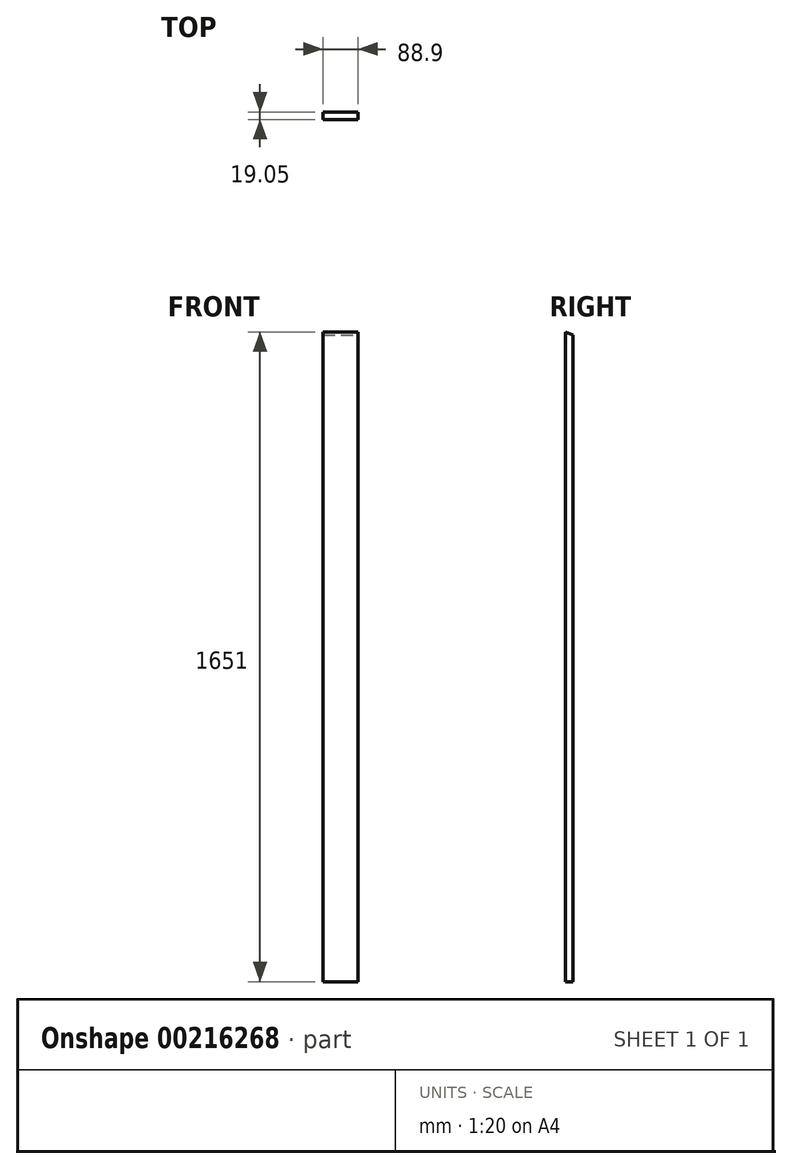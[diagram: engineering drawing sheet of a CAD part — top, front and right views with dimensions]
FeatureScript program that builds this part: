
annotation { "Feature Type Name" : "Feature", "Feature Type Description" : "" }
export const myFeature = defineFeature(function(context is Context, id is Id, definition is map)
    precondition{}
    {
        {
            var Q0;
            Q0=qCreatedBy(makeId("Front.planeOp"),FACE);
            var sketch = newSketch(context, id + "F0", { "sketchPlane" : qUnion([Q0])});
            skLineSegment(sketch, "E0", {"start": v(-3025.56, -1512.47) * mm, "end": v(-3114.46, -1512.47) * mm});
            skLineSegment(sketch, "E1", {"start": v(-3114.46, -1512.47) * mm, "end": v(-3114.46, 138.53) * mm});
            skLineSegment(sketch, "E2", {"start": v(-3114.46, 138.53) * mm, "end": v(-3025.56, 138.53) * mm});
            skLineSegment(sketch, "E3", {"start": v(-3025.56, 138.53) * mm, "end": v(-3025.56, -1512.47) * mm});
            skSolve(sketch);
        }
        {
            var Q0;
            Q0=makeQuery(id+"F0.imprint","IMPRINT",FACE,{"disambiguationData":[TD([[makeQuery(id+"F0.imprint","IMPRINT",EDGE,{"derivedFrom":sQuery(id+"F0.wireOp",EDGE,"E0")}),-1.0]])]});
            extrude(context, id + "F1", {"entities" : qUnion([Q0]), "depth" : 19.05 * mm});
        }
        {
            var Q0;
            Q0=makeQuery(id+"F1.opExtrude","SWEPT_FACE",FACE,{"disambiguationData":[OSD([sQuery(id+"F0.wireOp",EDGE,"E3")])]});
            var sketch = newSketch(context, id + "F2", { "sketchPlane" : qUnion([Q0])});
            skLineSegment(sketch, "E4", {"start": v(-19.05, 138.53) * mm, "end": v(0, 138.53) * mm});
            skLineSegment(sketch, "E5", {"start": v(0, 138.53) * mm, "end": v(0, 130.64) * mm});
            skLineSegment(sketch, "E6", {"start": v(0, 130.64) * mm, "end": v(-19.05, 138.53) * mm});
            skSolve(sketch);
        }
        {
            var Q0;
            Q0=makeQuery(id+"F2.imprint","IMPRINT",FACE,{"disambiguationData":[TD([[makeQuery(id+"F2.imprint","IMPRINT",EDGE,{"derivedFrom":sQuery(id+"F2.wireOp",EDGE,"E4")}),-1.0]])]});
            extrude(context, id + "F3", {"entities" : qUnion([Q0]), "operationType" : NewBodyOperationType.REMOVE, "endBound" : BoundingType.THROUGH_ALL, "oppositeDirection" : true, "depth" : 25.4 * mm});
        }
    });
